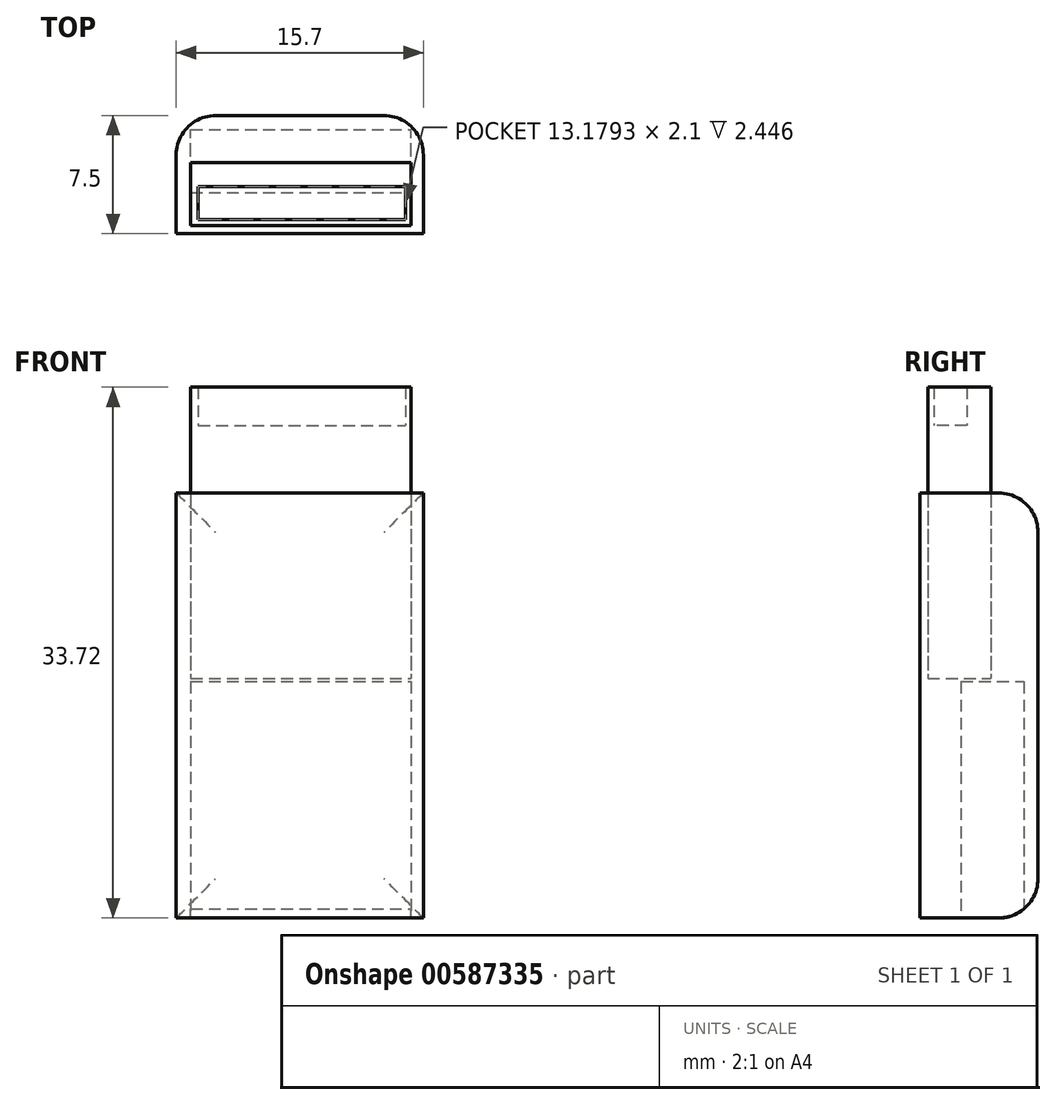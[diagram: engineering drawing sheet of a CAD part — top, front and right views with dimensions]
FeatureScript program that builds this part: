
annotation { "Feature Type Name" : "Feature", "Feature Type Description" : "" }
export const myFeature = defineFeature(function(context is Context, id is Id, definition is map)
    precondition{}
    {
        {
            var Q0;
            Q0=qCreatedBy(makeId("Front.planeOp"),FACE);
            var sketch = newSketch(context, id + "F0", { "sketchPlane" : qUnion([Q0])});
            skLineSegment(sketch, "E0.bottom", {"start": v(-53.62, 31.63) * mm, "end": v(-37.92, 31.63) * mm});
            skLineSegment(sketch, "E0.top", {"start": v(-53.62, 4.63) * mm, "end": v(-37.92, 4.63) * mm});
            skLineSegment(sketch, "E0.left", {"start": v(-53.62, 31.63) * mm, "end": v(-53.62, 4.63) * mm});
            skLineSegment(sketch, "E0.right", {"start": v(-37.92, 31.63) * mm, "end": v(-37.92, 4.63) * mm});
            skSolve(sketch);
        }
        {
            var Q0;
            Q0 = qSketchRegion(id + "F0", true);
            extrude(context, id + "F1", {"entities" : qUnion([Q0]), "depth" : 7.5 * mm, "offsetDistance" : 25 * mm});
        }
        {
            var Q0;
            Q0=qCreatedBy(makeId("Front.planeOp"),FACE);
            var sketch = newSketch(context, id + "F2", { "sketchPlane" : qUnion([Q0])});
            skLineSegment(sketch, "E1.bottom", {"start": v(-52.9, 4.45) * mm, "end": v(-38.9, 4.45) * mm});
            skLineSegment(sketch, "E1.top", {"start": v(-52.9, -14.06) * mm, "end": v(-38.9, -14.06) * mm});
            skLineSegment(sketch, "E1.left", {"start": v(-52.9, 4.45) * mm, "end": v(-52.9, -14.06) * mm});
            skLineSegment(sketch, "E1.right", {"start": v(-38.9, 4.45) * mm, "end": v(-38.9, -14.06) * mm});
            skSolve(sketch);
        }
        {
            var Q0;
            Q0 = qSketchRegion(id + "F2", true);
            extrude(context, id + "F3", {"entities" : qUnion([Q0]), "depth" : 4 * mm, "offsetDistance" : 25 * mm});
        }
        {
            var Q0;
            Q0=makeQuery(id+"F3.opExtrude","SWEPT_BODY",BODY,{"disambiguationData":[OSD([sQuery(id+"F2.wireOp",EDGE,"E1.bottom"),sQuery(id+"F2.wireOp",EDGE,"E1.top"),sQuery(id+"F2.wireOp",EDGE,"E1.left"),sQuery(id+"F2.wireOp",EDGE,"E1.right")])]});
            transform(context, id + "F4", {"entities" : qUnion([Q0]), "transformType" : TransformType.TRANSLATION_3D, "dx" : 0.2 * mm, "dy" : -0.9 * mm, "dz" : 15.2 * mm, "makeCopy" : false});
        }
        {
            var Q0;
            Q0=makeQuery(id+"F3.opExtrude","SWEPT_BODY",BODY,{"disambiguationData":[OSD([sQuery(id+"F2.wireOp",EDGE,"E1.bottom"),sQuery(id+"F2.wireOp",EDGE,"E1.top"),sQuery(id+"F2.wireOp",EDGE,"E1.left"),sQuery(id+"F2.wireOp",EDGE,"E1.right")])]});
            var Q1;
            Q1=makeQuery(id+"F1.opExtrude","SWEPT_BODY",BODY,{"disambiguationData":[OSD([sQuery(id+"F0.wireOp",EDGE,"E0.bottom"),sQuery(id+"F0.wireOp",EDGE,"E0.top"),sQuery(id+"F0.wireOp",EDGE,"E0.left"),sQuery(id+"F0.wireOp",EDGE,"E0.right")])]});
            booleanBodies(context, id + "F5", {"operationType" : BooleanOperationType.SUBTRACTION, "tools" : qUnion([Q0]), "targets" : qUnion([Q1]), "keepTools" : true});
        }
        {
            var Q0;
            Q0=makeQuery(id+"F3.opExtrude","SWEPT_BODY",BODY,{"disambiguationData":[OSD([sQuery(id+"F2.wireOp",EDGE,"E1.bottom"),sQuery(id+"F2.wireOp",EDGE,"E1.top"),sQuery(id+"F2.wireOp",EDGE,"E1.left"),sQuery(id+"F2.wireOp",EDGE,"E1.right")])]});
            transform(context, id + "F6", {"entities" : qUnion([Q0]), "transformType" : TransformType.TRANSLATION_3D, "dx" : 0 * mm, "dy" : -2.1 * mm, "dz" : 18.7 * mm, "makeCopy" : false});
        }
        {
            var Q0;
            Q0=makeQuery(id+"F1.opExtrude","CAP_FACE",FACE,{"disambiguationData":[OSD([sQuery(id+"F0.wireOp",EDGE,"E0.bottom"),sQuery(id+"F0.wireOp",EDGE,"E0.top"),sQuery(id+"F0.wireOp",EDGE,"E0.left"),sQuery(id+"F0.wireOp",EDGE,"E0.right")])],"isStart":true});
            fillet(context, id + "F7", {"entities" : qUnion([Q0]), "radius" : 2.5 * mm, "tangentPropagation" : true, "allowEdgeOverflow" : false});
        }
        {
            var Q0;
            Q0=qCreatedBy(makeId("Top.planeOp"),FACE);
            var sketch = newSketch(context, id + "F8", { "sketchPlane" : qUnion([Q0])});
            skLineSegment(sketch, "E2.bottom", {"start": v(-52.22, -4.52) * mm, "end": v(-39.05, -4.52) * mm});
            skLineSegment(sketch, "E2.top", {"start": v(-52.22, -6.62) * mm, "end": v(-39.05, -6.62) * mm});
            skLineSegment(sketch, "E2.left", {"start": v(-52.22, -4.52) * mm, "end": v(-52.22, -6.62) * mm});
            skLineSegment(sketch, "E2.right", {"start": v(-39.05, -4.52) * mm, "end": v(-39.05, -6.62) * mm});
            skSolve(sketch);
        }
        {
            var Q0;
            Q0 = qSketchRegion(id + "F8", true);
            extrude(context, id + "F9", {"entities" : qUnion([Q0]), "depth" : 7.5 * mm, "offsetDistance" : 25 * mm});
        }
        {
            var Q0;
            Q0=makeQuery(id+"F9.opExtrude","SWEPT_BODY",BODY,{"disambiguationData":[OSD([sQuery(id+"F8.wireOp",EDGE,"E2.bottom"),sQuery(id+"F8.wireOp",EDGE,"E2.top"),sQuery(id+"F8.wireOp",EDGE,"E2.left"),sQuery(id+"F8.wireOp",EDGE,"E2.right")])]});
            transform(context, id + "F10", {"entities" : qUnion([Q0]), "transformType" : TransformType.TRANSLATION_3D, "dx" : 0 * mm, "dy" : 0 * mm, "dz" : 35.9 * mm, "makeCopy" : false});
        }
        {
            var Q0;
            Q0=makeQuery(id+"F9.opExtrude","SWEPT_BODY",BODY,{"disambiguationData":[OSD([sQuery(id+"F8.wireOp",EDGE,"E2.bottom"),sQuery(id+"F8.wireOp",EDGE,"E2.top"),sQuery(id+"F8.wireOp",EDGE,"E2.left"),sQuery(id+"F8.wireOp",EDGE,"E2.right")])]});
            var Q1;
            Q1=makeQuery(id+"F3.opExtrude","SWEPT_BODY",BODY,{"disambiguationData":[OSD([sQuery(id+"F2.wireOp",EDGE,"E1.bottom"),sQuery(id+"F2.wireOp",EDGE,"E1.top"),sQuery(id+"F2.wireOp",EDGE,"E1.left"),sQuery(id+"F2.wireOp",EDGE,"E1.right")])]});
            booleanBodies(context, id + "F11", {"operationType" : BooleanOperationType.SUBTRACTION, "tools" : qUnion([Q0]), "targets" : qUnion([Q1])});
        }
    });
